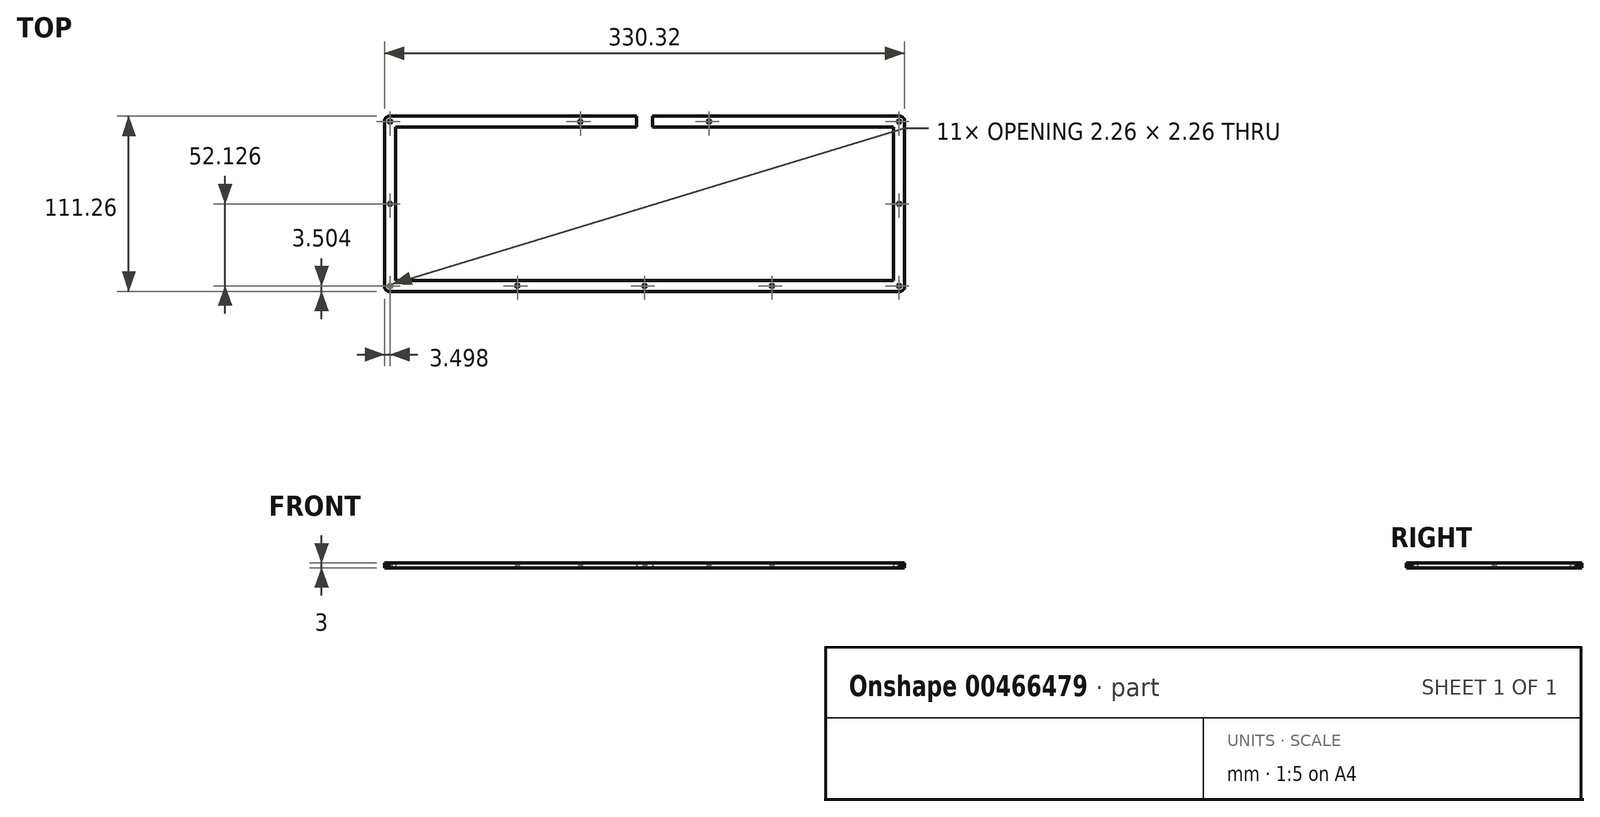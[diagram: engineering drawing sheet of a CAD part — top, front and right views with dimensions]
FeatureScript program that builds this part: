
annotation { "Feature Type Name" : "Feature", "Feature Type Description" : "" }
export const myFeature = defineFeature(function(context is Context, id is Id, definition is map)
    precondition{}
    {
        {
            var Q0;
            Q0=qCreatedBy(makeId("Top.planeOp"),FACE);
            var sketch = newSketch(context, id + "F0", { "sketchPlane" : qUnion([Q0])});
            skLineSegment(sketch, "E0", {"start": v(-5, 55.63) * mm, "end": v(-5, 48.62) * mm});
            skLineSegment(sketch, "E1", {"start": v(-5, 48.62) * mm, "end": v(-158.16, 48.62) * mm});
            skLineSegment(sketch, "E2", {"start": v(-158.16, 48.62) * mm, "end": v(-158.16, -48.63) * mm});
            skLineSegment(sketch, "E3", {"start": v(-158.16, -48.63) * mm, "end": v(158.16, -48.63) * mm});
            skLineSegment(sketch, "E4", {"start": v(158.16, -48.63) * mm, "end": v(158.16, 48.62) * mm});
            skLineSegment(sketch, "E5", {"start": v(158.16, 48.62) * mm, "end": v(5, 48.62) * mm});
            skLineSegment(sketch, "E6", {"start": v(5, 48.62) * mm, "end": v(5, 55.62) * mm});
            skLineSegment(sketch, "E7", {"start": v(5, 55.62) * mm, "end": v(162.16, 55.62) * mm});
            skLineSegment(sketch, "E8", {"start": v(162.16, 55.62) * mm, "end": v(162.4, 55.62) * mm});
            skLineSegment(sketch, "E9", {"start": v(162.4, 55.62) * mm, "end": v(162.63, 55.59) * mm});
            skLineSegment(sketch, "E10", {"start": v(162.63, 55.59) * mm, "end": v(162.86, 55.54) * mm});
            skLineSegment(sketch, "E11", {"start": v(162.86, 55.54) * mm, "end": v(163.1, 55.48) * mm});
            skLineSegment(sketch, "E12", {"start": v(163.1, 55.48) * mm, "end": v(163.31, 55.4) * mm});
            skLineSegment(sketch, "E13", {"start": v(163.31, 55.4) * mm, "end": v(163.53, 55.3) * mm});
            skLineSegment(sketch, "E14", {"start": v(163.53, 55.3) * mm, "end": v(163.73, 55.18) * mm});
            skLineSegment(sketch, "E15", {"start": v(163.73, 55.18) * mm, "end": v(163.93, 55.05) * mm});
            skLineSegment(sketch, "E16", {"start": v(163.93, 55.05) * mm, "end": v(164.11, 54.9) * mm});
            skLineSegment(sketch, "E17", {"start": v(164.11, 54.9) * mm, "end": v(164.29, 54.75) * mm});
            skLineSegment(sketch, "E18", {"start": v(164.29, 54.75) * mm, "end": v(164.45, 54.57) * mm});
            skLineSegment(sketch, "E19", {"start": v(164.45, 54.57) * mm, "end": v(164.6, 54.39) * mm});
            skLineSegment(sketch, "E20", {"start": v(164.6, 54.39) * mm, "end": v(164.72, 54.2) * mm});
            skLineSegment(sketch, "E21", {"start": v(164.72, 54.2) * mm, "end": v(164.84, 53.99) * mm});
            skLineSegment(sketch, "E22", {"start": v(164.84, 53.99) * mm, "end": v(164.93, 53.77) * mm});
            skLineSegment(sketch, "E23", {"start": v(164.93, 53.77) * mm, "end": v(165.02, 53.55) * mm});
            skLineSegment(sketch, "E24", {"start": v(165.02, 53.55) * mm, "end": v(165.08, 53.33) * mm});
            skLineSegment(sketch, "E25", {"start": v(165.08, 53.33) * mm, "end": v(165.13, 53.1) * mm});
            skLineSegment(sketch, "E26", {"start": v(165.13, 53.1) * mm, "end": v(165.15, 52.86) * mm});
            skLineSegment(sketch, "E27", {"start": v(165.15, 52.86) * mm, "end": v(165.16, 52.62) * mm});
            skLineSegment(sketch, "E28", {"start": v(165.16, 52.62) * mm, "end": v(165.16, -52.63) * mm});
            skLineSegment(sketch, "E29", {"start": v(165.16, -52.63) * mm, "end": v(165.15, -52.86) * mm});
            skLineSegment(sketch, "E30", {"start": v(165.15, -52.86) * mm, "end": v(165.13, -53.1) * mm});
            skLineSegment(sketch, "E31", {"start": v(165.13, -53.1) * mm, "end": v(165.08, -53.33) * mm});
            skLineSegment(sketch, "E32", {"start": v(165.08, -53.33) * mm, "end": v(165.02, -53.55) * mm});
            skLineSegment(sketch, "E33", {"start": v(165.02, -53.55) * mm, "end": v(164.93, -53.77) * mm});
            skLineSegment(sketch, "E34", {"start": v(164.93, -53.77) * mm, "end": v(164.84, -53.99) * mm});
            skLineSegment(sketch, "E35", {"start": v(164.84, -53.99) * mm, "end": v(164.72, -54.2) * mm});
            skLineSegment(sketch, "E36", {"start": v(164.72, -54.2) * mm, "end": v(164.6, -54.39) * mm});
            skLineSegment(sketch, "E37", {"start": v(164.6, -54.39) * mm, "end": v(164.45, -54.57) * mm});
            skLineSegment(sketch, "E38", {"start": v(164.45, -54.57) * mm, "end": v(164.29, -54.75) * mm});
            skLineSegment(sketch, "E39", {"start": v(164.29, -54.75) * mm, "end": v(164.11, -54.9) * mm});
            skLineSegment(sketch, "E40", {"start": v(164.11, -54.9) * mm, "end": v(163.93, -55.05) * mm});
            skLineSegment(sketch, "E41", {"start": v(163.93, -55.05) * mm, "end": v(163.73, -55.18) * mm});
            skLineSegment(sketch, "E42", {"start": v(163.73, -55.18) * mm, "end": v(163.53, -55.3) * mm});
            skLineSegment(sketch, "E43", {"start": v(163.53, -55.3) * mm, "end": v(163.31, -55.4) * mm});
            skLineSegment(sketch, "E44", {"start": v(163.31, -55.4) * mm, "end": v(163.1, -55.48) * mm});
            skLineSegment(sketch, "E45", {"start": v(163.1, -55.48) * mm, "end": v(162.86, -55.54) * mm});
            skLineSegment(sketch, "E46", {"start": v(162.86, -55.54) * mm, "end": v(162.63, -55.59) * mm});
            skLineSegment(sketch, "E47", {"start": v(162.63, -55.59) * mm, "end": v(162.4, -55.62) * mm});
            skLineSegment(sketch, "E48", {"start": v(162.4, -55.62) * mm, "end": v(162.16, -55.63) * mm});
            skLineSegment(sketch, "E49", {"start": v(162.16, -55.63) * mm, "end": v(-162.16, -55.63) * mm});
            skLineSegment(sketch, "E50", {"start": v(-162.16, -55.63) * mm, "end": v(-162.4, -55.62) * mm});
            skLineSegment(sketch, "E51", {"start": v(-162.4, -55.62) * mm, "end": v(-162.63, -55.59) * mm});
            skLineSegment(sketch, "E52", {"start": v(-162.63, -55.59) * mm, "end": v(-162.86, -55.54) * mm});
            skLineSegment(sketch, "E53", {"start": v(-162.86, -55.54) * mm, "end": v(-163.09, -55.48) * mm});
            skLineSegment(sketch, "E54", {"start": v(-163.09, -55.48) * mm, "end": v(-163.31, -55.4) * mm});
            skLineSegment(sketch, "E55", {"start": v(-163.31, -55.4) * mm, "end": v(-163.52, -55.3) * mm});
            skLineSegment(sketch, "E56", {"start": v(-163.52, -55.3) * mm, "end": v(-163.73, -55.18) * mm});
            skLineSegment(sketch, "E57", {"start": v(-163.73, -55.18) * mm, "end": v(-163.93, -55.05) * mm});
            skLineSegment(sketch, "E58", {"start": v(-163.93, -55.05) * mm, "end": v(-164.11, -54.9) * mm});
            skLineSegment(sketch, "E59", {"start": v(-164.11, -54.9) * mm, "end": v(-164.28, -54.75) * mm});
            skLineSegment(sketch, "E60", {"start": v(-164.28, -54.75) * mm, "end": v(-164.44, -54.57) * mm});
            skLineSegment(sketch, "E61", {"start": v(-164.44, -54.57) * mm, "end": v(-164.6, -54.39) * mm});
            skLineSegment(sketch, "E62", {"start": v(-164.6, -54.39) * mm, "end": v(-164.72, -54.2) * mm});
            skLineSegment(sketch, "E63", {"start": v(-164.72, -54.2) * mm, "end": v(-164.84, -53.99) * mm});
            skLineSegment(sketch, "E64", {"start": v(-164.84, -53.99) * mm, "end": v(-164.93, -53.77) * mm});
            skLineSegment(sketch, "E65", {"start": v(-164.93, -53.77) * mm, "end": v(-165.02, -53.55) * mm});
            skLineSegment(sketch, "E66", {"start": v(-165.02, -53.55) * mm, "end": v(-165.08, -53.33) * mm});
            skLineSegment(sketch, "E67", {"start": v(-165.08, -53.33) * mm, "end": v(-165.13, -53.1) * mm});
            skLineSegment(sketch, "E68", {"start": v(-165.13, -53.1) * mm, "end": v(-165.15, -52.86) * mm});
            skLineSegment(sketch, "E69", {"start": v(-165.15, -52.86) * mm, "end": v(-165.16, -52.63) * mm});
            skLineSegment(sketch, "E70", {"start": v(-165.16, -52.63) * mm, "end": v(-165.16, 52.62) * mm});
            skLineSegment(sketch, "E71", {"start": v(-165.16, 52.62) * mm, "end": v(-165.15, 52.86) * mm});
            skLineSegment(sketch, "E72", {"start": v(-165.15, 52.86) * mm, "end": v(-165.13, 53.1) * mm});
            skLineSegment(sketch, "E73", {"start": v(-165.13, 53.1) * mm, "end": v(-165.08, 53.33) * mm});
            skLineSegment(sketch, "E74", {"start": v(-165.08, 53.33) * mm, "end": v(-165.02, 53.55) * mm});
            skLineSegment(sketch, "E75", {"start": v(-165.02, 53.55) * mm, "end": v(-164.93, 53.77) * mm});
            skLineSegment(sketch, "E76", {"start": v(-164.93, 53.77) * mm, "end": v(-164.84, 53.99) * mm});
            skLineSegment(sketch, "E77", {"start": v(-164.84, 53.99) * mm, "end": v(-164.72, 54.2) * mm});
            skLineSegment(sketch, "E78", {"start": v(-164.72, 54.2) * mm, "end": v(-164.6, 54.39) * mm});
            skLineSegment(sketch, "E79", {"start": v(-164.6, 54.39) * mm, "end": v(-164.44, 54.57) * mm});
            skLineSegment(sketch, "E80", {"start": v(-164.44, 54.57) * mm, "end": v(-164.28, 54.75) * mm});
            skLineSegment(sketch, "E81", {"start": v(-164.28, 54.75) * mm, "end": v(-164.11, 54.9) * mm});
            skLineSegment(sketch, "E82", {"start": v(-164.11, 54.9) * mm, "end": v(-163.93, 55.05) * mm});
            skLineSegment(sketch, "E83", {"start": v(-163.93, 55.05) * mm, "end": v(-163.73, 55.18) * mm});
            skLineSegment(sketch, "E84", {"start": v(-163.73, 55.18) * mm, "end": v(-163.52, 55.3) * mm});
            skLineSegment(sketch, "E85", {"start": v(-163.52, 55.3) * mm, "end": v(-163.31, 55.4) * mm});
            skLineSegment(sketch, "E86", {"start": v(-163.31, 55.4) * mm, "end": v(-163.09, 55.48) * mm});
            skLineSegment(sketch, "E87", {"start": v(-163.09, 55.48) * mm, "end": v(-162.86, 55.54) * mm});
            skLineSegment(sketch, "E88", {"start": v(-162.86, 55.54) * mm, "end": v(-162.63, 55.59) * mm});
            skLineSegment(sketch, "E89", {"start": v(-162.63, 55.59) * mm, "end": v(-162.4, 55.62) * mm});
            skLineSegment(sketch, "E90", {"start": v(-162.4, 55.62) * mm, "end": v(-162.16, 55.63) * mm});
            skLineSegment(sketch, "E91", {"start": v(-162.16, 55.63) * mm, "end": v(-5, 55.63) * mm});
            skLineSegment(sketch, "E92", {"start": v(161.31, -51.05) * mm, "end": v(161, -51.21) * mm});
            skLineSegment(sketch, "E93", {"start": v(161, -51.21) * mm, "end": v(160.75, -51.46) * mm});
            skLineSegment(sketch, "E94", {"start": v(160.75, -51.46) * mm, "end": v(160.59, -51.78) * mm});
            skLineSegment(sketch, "E95", {"start": v(160.59, -51.78) * mm, "end": v(160.53, -52.13) * mm});
            skLineSegment(sketch, "E96", {"start": v(160.53, -52.13) * mm, "end": v(160.59, -52.48) * mm});
            skLineSegment(sketch, "E97", {"start": v(160.59, -52.48) * mm, "end": v(160.75, -52.79) * mm});
            skLineSegment(sketch, "E98", {"start": v(160.75, -52.79) * mm, "end": v(161, -53.04) * mm});
            skLineSegment(sketch, "E99", {"start": v(161, -53.04) * mm, "end": v(161.31, -53.2) * mm});
            skLineSegment(sketch, "E100", {"start": v(161.31, -53.2) * mm, "end": v(161.66, -53.26) * mm});
            skLineSegment(sketch, "E101", {"start": v(161.66, -53.26) * mm, "end": v(162.01, -53.2) * mm});
            skLineSegment(sketch, "E102", {"start": v(162.01, -53.2) * mm, "end": v(162.33, -53.04) * mm});
            skLineSegment(sketch, "E103", {"start": v(162.33, -53.04) * mm, "end": v(162.58, -52.79) * mm});
            skLineSegment(sketch, "E104", {"start": v(162.58, -52.79) * mm, "end": v(162.74, -52.48) * mm});
            skLineSegment(sketch, "E105", {"start": v(162.74, -52.48) * mm, "end": v(162.8, -52.13) * mm});
            skLineSegment(sketch, "E106", {"start": v(162.8, -52.13) * mm, "end": v(162.74, -51.78) * mm});
            skLineSegment(sketch, "E107", {"start": v(162.74, -51.78) * mm, "end": v(162.58, -51.46) * mm});
            skLineSegment(sketch, "E108", {"start": v(162.58, -51.46) * mm, "end": v(162.33, -51.21) * mm});
            skLineSegment(sketch, "E109", {"start": v(162.33, -51.21) * mm, "end": v(162.01, -51.05) * mm});
            skLineSegment(sketch, "E110", {"start": v(162.01, -51.05) * mm, "end": v(161.66, -51) * mm});
            skLineSegment(sketch, "E111", {"start": v(161.66, -51) * mm, "end": v(161.31, -51.05) * mm});
            skLineSegment(sketch, "E112", {"start": v(80.48, -51.05) * mm, "end": v(80.17, -51.21) * mm});
            skLineSegment(sketch, "E113", {"start": v(80.17, -51.21) * mm, "end": v(79.92, -51.46) * mm});
            skLineSegment(sketch, "E114", {"start": v(79.92, -51.46) * mm, "end": v(79.76, -51.78) * mm});
            skLineSegment(sketch, "E115", {"start": v(79.76, -51.78) * mm, "end": v(79.7, -52.13) * mm});
            skLineSegment(sketch, "E116", {"start": v(79.7, -52.13) * mm, "end": v(79.76, -52.48) * mm});
            skLineSegment(sketch, "E117", {"start": v(79.76, -52.48) * mm, "end": v(79.92, -52.79) * mm});
            skLineSegment(sketch, "E118", {"start": v(79.92, -52.79) * mm, "end": v(80.17, -53.04) * mm});
            skLineSegment(sketch, "E119", {"start": v(80.17, -53.04) * mm, "end": v(80.48, -53.2) * mm});
            skLineSegment(sketch, "E120", {"start": v(80.48, -53.2) * mm, "end": v(80.83, -53.26) * mm});
            skLineSegment(sketch, "E121", {"start": v(80.83, -53.26) * mm, "end": v(81.18, -53.2) * mm});
            skLineSegment(sketch, "E122", {"start": v(81.18, -53.2) * mm, "end": v(81.5, -53.04) * mm});
            skLineSegment(sketch, "E123", {"start": v(81.5, -53.04) * mm, "end": v(81.75, -52.79) * mm});
            skLineSegment(sketch, "E124", {"start": v(81.75, -52.79) * mm, "end": v(81.9, -52.48) * mm});
            skLineSegment(sketch, "E125", {"start": v(81.9, -52.48) * mm, "end": v(81.96, -52.13) * mm});
            skLineSegment(sketch, "E126", {"start": v(81.96, -52.13) * mm, "end": v(81.9, -51.78) * mm});
            skLineSegment(sketch, "E127", {"start": v(81.9, -51.78) * mm, "end": v(81.75, -51.46) * mm});
            skLineSegment(sketch, "E128", {"start": v(81.75, -51.46) * mm, "end": v(81.5, -51.21) * mm});
            skLineSegment(sketch, "E129", {"start": v(81.5, -51.21) * mm, "end": v(81.18, -51.05) * mm});
            skLineSegment(sketch, "E130", {"start": v(81.18, -51.05) * mm, "end": v(80.83, -51) * mm});
            skLineSegment(sketch, "E131", {"start": v(80.83, -51) * mm, "end": v(80.48, -51.05) * mm});
            skLineSegment(sketch, "E132", {"start": v(-0.35, -51.05) * mm, "end": v(-0.66, -51.21) * mm});
            skLineSegment(sketch, "E133", {"start": v(-0.66, -51.21) * mm, "end": v(-0.91, -51.46) * mm});
            skLineSegment(sketch, "E134", {"start": v(-0.91, -51.46) * mm, "end": v(-1.07, -51.78) * mm});
            skLineSegment(sketch, "E135", {"start": v(-1.07, -51.78) * mm, "end": v(-1.13, -52.13) * mm});
            skLineSegment(sketch, "E136", {"start": v(-1.13, -52.13) * mm, "end": v(-1.07, -52.48) * mm});
            skLineSegment(sketch, "E137", {"start": v(-1.07, -52.48) * mm, "end": v(-0.91, -52.79) * mm});
            skLineSegment(sketch, "E138", {"start": v(-0.91, -52.79) * mm, "end": v(-0.66, -53.04) * mm});
            skLineSegment(sketch, "E139", {"start": v(-0.66, -53.04) * mm, "end": v(-0.35, -53.2) * mm});
            skLineSegment(sketch, "E140", {"start": v(-0.35, -53.2) * mm, "end": v(0, -53.26) * mm});
            skLineSegment(sketch, "E141", {"start": v(0, -53.26) * mm, "end": v(0.35, -53.2) * mm});
            skLineSegment(sketch, "E142", {"start": v(0.35, -53.2) * mm, "end": v(0.67, -53.04) * mm});
            skLineSegment(sketch, "E143", {"start": v(0.67, -53.04) * mm, "end": v(0.92, -52.79) * mm});
            skLineSegment(sketch, "E144", {"start": v(0.92, -52.79) * mm, "end": v(1.07, -52.48) * mm});
            skLineSegment(sketch, "E145", {"start": v(1.07, -52.48) * mm, "end": v(1.13, -52.13) * mm});
            skLineSegment(sketch, "E146", {"start": v(1.13, -52.13) * mm, "end": v(1.07, -51.78) * mm});
            skLineSegment(sketch, "E147", {"start": v(1.07, -51.78) * mm, "end": v(0.92, -51.46) * mm});
            skLineSegment(sketch, "E148", {"start": v(0.92, -51.46) * mm, "end": v(0.67, -51.21) * mm});
            skLineSegment(sketch, "E149", {"start": v(0.67, -51.21) * mm, "end": v(0.35, -51.05) * mm});
            skLineSegment(sketch, "E150", {"start": v(0.35, -51.05) * mm, "end": v(0, -51) * mm});
            skLineSegment(sketch, "E151", {"start": v(0, -51) * mm, "end": v(-0.35, -51.05) * mm});
            skLineSegment(sketch, "E152", {"start": v(-81.18, -51.05) * mm, "end": v(-81.5, -51.21) * mm});
            skLineSegment(sketch, "E153", {"start": v(-81.5, -51.21) * mm, "end": v(-81.75, -51.46) * mm});
            skLineSegment(sketch, "E154", {"start": v(-81.75, -51.46) * mm, "end": v(-81.9, -51.78) * mm});
            skLineSegment(sketch, "E155", {"start": v(-81.9, -51.78) * mm, "end": v(-81.96, -52.13) * mm});
            skLineSegment(sketch, "E156", {"start": v(-81.96, -52.13) * mm, "end": v(-81.9, -52.48) * mm});
            skLineSegment(sketch, "E157", {"start": v(-81.9, -52.48) * mm, "end": v(-81.75, -52.79) * mm});
            skLineSegment(sketch, "E158", {"start": v(-81.75, -52.79) * mm, "end": v(-81.5, -53.04) * mm});
            skLineSegment(sketch, "E159", {"start": v(-81.5, -53.04) * mm, "end": v(-81.18, -53.2) * mm});
            skLineSegment(sketch, "E160", {"start": v(-81.18, -53.2) * mm, "end": v(-80.83, -53.26) * mm});
            skLineSegment(sketch, "E161", {"start": v(-80.83, -53.26) * mm, "end": v(-80.48, -53.2) * mm});
            skLineSegment(sketch, "E162", {"start": v(-80.48, -53.2) * mm, "end": v(-80.17, -53.04) * mm});
            skLineSegment(sketch, "E163", {"start": v(-80.17, -53.04) * mm, "end": v(-79.92, -52.79) * mm});
            skLineSegment(sketch, "E164", {"start": v(-79.92, -52.79) * mm, "end": v(-79.76, -52.48) * mm});
            skLineSegment(sketch, "E165", {"start": v(-79.76, -52.48) * mm, "end": v(-79.7, -52.13) * mm});
            skLineSegment(sketch, "E166", {"start": v(-79.7, -52.13) * mm, "end": v(-79.76, -51.78) * mm});
            skLineSegment(sketch, "E167", {"start": v(-79.76, -51.78) * mm, "end": v(-79.92, -51.46) * mm});
            skLineSegment(sketch, "E168", {"start": v(-79.92, -51.46) * mm, "end": v(-80.17, -51.21) * mm});
            skLineSegment(sketch, "E169", {"start": v(-80.17, -51.21) * mm, "end": v(-80.48, -51.05) * mm});
            skLineSegment(sketch, "E170", {"start": v(-80.48, -51.05) * mm, "end": v(-80.83, -51) * mm});
            skLineSegment(sketch, "E171", {"start": v(-80.83, -51) * mm, "end": v(-81.18, -51.05) * mm});
            skLineSegment(sketch, "E172", {"start": v(-162.01, -51.05) * mm, "end": v(-162.33, -51.21) * mm});
            skLineSegment(sketch, "E173", {"start": v(-162.33, -51.21) * mm, "end": v(-162.58, -51.46) * mm});
            skLineSegment(sketch, "E174", {"start": v(-162.58, -51.46) * mm, "end": v(-162.74, -51.78) * mm});
            skLineSegment(sketch, "E175", {"start": v(-162.74, -51.78) * mm, "end": v(-162.8, -52.13) * mm});
            skLineSegment(sketch, "E176", {"start": v(-162.8, -52.13) * mm, "end": v(-162.74, -52.48) * mm});
            skLineSegment(sketch, "E177", {"start": v(-162.74, -52.48) * mm, "end": v(-162.58, -52.79) * mm});
            skLineSegment(sketch, "E178", {"start": v(-162.58, -52.79) * mm, "end": v(-162.33, -53.04) * mm});
            skLineSegment(sketch, "E179", {"start": v(-162.33, -53.04) * mm, "end": v(-162.01, -53.2) * mm});
            skLineSegment(sketch, "E180", {"start": v(-162.01, -53.2) * mm, "end": v(-161.66, -53.26) * mm});
            skLineSegment(sketch, "E181", {"start": v(-161.66, -53.26) * mm, "end": v(-161.31, -53.2) * mm});
            skLineSegment(sketch, "E182", {"start": v(-161.31, -53.2) * mm, "end": v(-161, -53.04) * mm});
            skLineSegment(sketch, "E183", {"start": v(-161, -53.04) * mm, "end": v(-160.75, -52.79) * mm});
            skLineSegment(sketch, "E184", {"start": v(-160.75, -52.79) * mm, "end": v(-160.59, -52.48) * mm});
            skLineSegment(sketch, "E185", {"start": v(-160.59, -52.48) * mm, "end": v(-160.53, -52.13) * mm});
            skLineSegment(sketch, "E186", {"start": v(-160.53, -52.13) * mm, "end": v(-160.59, -51.78) * mm});
            skLineSegment(sketch, "E187", {"start": v(-160.59, -51.78) * mm, "end": v(-160.75, -51.46) * mm});
            skLineSegment(sketch, "E188", {"start": v(-160.75, -51.46) * mm, "end": v(-161, -51.21) * mm});
            skLineSegment(sketch, "E189", {"start": v(-161, -51.21) * mm, "end": v(-161.31, -51.05) * mm});
            skLineSegment(sketch, "E190", {"start": v(-161.31, -51.05) * mm, "end": v(-161.66, -51) * mm});
            skLineSegment(sketch, "E191", {"start": v(-161.66, -51) * mm, "end": v(-162.01, -51.05) * mm});
            skLineSegment(sketch, "E192", {"start": v(161.31, 1.08) * mm, "end": v(161, 0.91) * mm});
            skLineSegment(sketch, "E193", {"start": v(161, 0.91) * mm, "end": v(160.75, 0.66) * mm});
            skLineSegment(sketch, "E194", {"start": v(160.75, 0.66) * mm, "end": v(160.59, 0.35) * mm});
            skLineSegment(sketch, "E195", {"start": v(160.59, 0.35) * mm, "end": v(160.53, 0) * mm});
            skLineSegment(sketch, "E196", {"start": v(160.53, 0) * mm, "end": v(160.59, -0.35) * mm});
            skLineSegment(sketch, "E197", {"start": v(160.59, -0.35) * mm, "end": v(160.75, -0.66) * mm});
            skLineSegment(sketch, "E198", {"start": v(160.75, -0.66) * mm, "end": v(161, -0.91) * mm});
            skLineSegment(sketch, "E199", {"start": v(161, -0.91) * mm, "end": v(161.31, -1.07) * mm});
            skLineSegment(sketch, "E200", {"start": v(161.31, -1.07) * mm, "end": v(161.66, -1.13) * mm});
            skLineSegment(sketch, "E201", {"start": v(161.66, -1.13) * mm, "end": v(162.01, -1.07) * mm});
            skLineSegment(sketch, "E202", {"start": v(162.01, -1.07) * mm, "end": v(162.33, -0.91) * mm});
            skLineSegment(sketch, "E203", {"start": v(162.33, -0.91) * mm, "end": v(162.58, -0.66) * mm});
            skLineSegment(sketch, "E204", {"start": v(162.58, -0.66) * mm, "end": v(162.74, -0.35) * mm});
            skLineSegment(sketch, "E205", {"start": v(162.74, -0.35) * mm, "end": v(162.8, 0) * mm});
            skLineSegment(sketch, "E206", {"start": v(162.8, 0) * mm, "end": v(162.74, 0.35) * mm});
            skLineSegment(sketch, "E207", {"start": v(162.74, 0.35) * mm, "end": v(162.58, 0.66) * mm});
            skLineSegment(sketch, "E208", {"start": v(162.58, 0.66) * mm, "end": v(162.33, 0.91) * mm});
            skLineSegment(sketch, "E209", {"start": v(162.33, 0.91) * mm, "end": v(162.01, 1.08) * mm});
            skLineSegment(sketch, "E210", {"start": v(162.01, 1.08) * mm, "end": v(161.66, 1.13) * mm});
            skLineSegment(sketch, "E211", {"start": v(161.66, 1.13) * mm, "end": v(161.31, 1.08) * mm});
            skLineSegment(sketch, "E212", {"start": v(-162.01, 1.08) * mm, "end": v(-162.33, 0.91) * mm});
            skLineSegment(sketch, "E213", {"start": v(-162.33, 0.91) * mm, "end": v(-162.58, 0.66) * mm});
            skLineSegment(sketch, "E214", {"start": v(-162.58, 0.66) * mm, "end": v(-162.74, 0.35) * mm});
            skLineSegment(sketch, "E215", {"start": v(-162.74, 0.35) * mm, "end": v(-162.8, 0) * mm});
            skLineSegment(sketch, "E216", {"start": v(-162.8, 0) * mm, "end": v(-162.74, -0.35) * mm});
            skLineSegment(sketch, "E217", {"start": v(-162.74, -0.35) * mm, "end": v(-162.58, -0.66) * mm});
            skLineSegment(sketch, "E218", {"start": v(-162.58, -0.66) * mm, "end": v(-162.33, -0.91) * mm});
            skLineSegment(sketch, "E219", {"start": v(-162.33, -0.91) * mm, "end": v(-162.01, -1.07) * mm});
            skLineSegment(sketch, "E220", {"start": v(-162.01, -1.07) * mm, "end": v(-161.66, -1.13) * mm});
            skLineSegment(sketch, "E221", {"start": v(-161.66, -1.13) * mm, "end": v(-161.31, -1.07) * mm});
            skLineSegment(sketch, "E222", {"start": v(-161.31, -1.07) * mm, "end": v(-161, -0.91) * mm});
            skLineSegment(sketch, "E223", {"start": v(-161, -0.91) * mm, "end": v(-160.75, -0.66) * mm});
            skLineSegment(sketch, "E224", {"start": v(-160.75, -0.66) * mm, "end": v(-160.59, -0.35) * mm});
            skLineSegment(sketch, "E225", {"start": v(-160.59, -0.35) * mm, "end": v(-160.53, 0) * mm});
            skLineSegment(sketch, "E226", {"start": v(-160.53, 0) * mm, "end": v(-160.59, 0.35) * mm});
            skLineSegment(sketch, "E227", {"start": v(-160.59, 0.35) * mm, "end": v(-160.75, 0.66) * mm});
            skLineSegment(sketch, "E228", {"start": v(-160.75, 0.66) * mm, "end": v(-161, 0.91) * mm});
            skLineSegment(sketch, "E229", {"start": v(-161, 0.91) * mm, "end": v(-161.31, 1.08) * mm});
            skLineSegment(sketch, "E230", {"start": v(-161.31, 1.08) * mm, "end": v(-161.66, 1.13) * mm});
            skLineSegment(sketch, "E231", {"start": v(-161.66, 1.13) * mm, "end": v(-162.01, 1.08) * mm});
            skLineSegment(sketch, "E232", {"start": v(-41.18, 53.2) * mm, "end": v(-41.5, 53.04) * mm});
            skLineSegment(sketch, "E233", {"start": v(-41.5, 53.04) * mm, "end": v(-41.75, 52.8) * mm});
            skLineSegment(sketch, "E234", {"start": v(-41.75, 52.8) * mm, "end": v(-41.9, 52.47) * mm});
            skLineSegment(sketch, "E235", {"start": v(-41.9, 52.47) * mm, "end": v(-41.96, 52.12) * mm});
            skLineSegment(sketch, "E236", {"start": v(-41.96, 52.12) * mm, "end": v(-41.9, 51.78) * mm});
            skLineSegment(sketch, "E237", {"start": v(-41.9, 51.78) * mm, "end": v(-41.75, 51.46) * mm});
            skLineSegment(sketch, "E238", {"start": v(-41.75, 51.46) * mm, "end": v(-41.5, 51.21) * mm});
            skLineSegment(sketch, "E239", {"start": v(-41.5, 51.21) * mm, "end": v(-41.18, 51.05) * mm});
            skLineSegment(sketch, "E240", {"start": v(-41.18, 51.05) * mm, "end": v(-40.83, 51) * mm});
            skLineSegment(sketch, "E241", {"start": v(-40.83, 51) * mm, "end": v(-40.48, 51.05) * mm});
            skLineSegment(sketch, "E242", {"start": v(-40.48, 51.05) * mm, "end": v(-40.17, 51.21) * mm});
            skLineSegment(sketch, "E243", {"start": v(-40.17, 51.21) * mm, "end": v(-39.92, 51.46) * mm});
            skLineSegment(sketch, "E244", {"start": v(-39.92, 51.46) * mm, "end": v(-39.76, 51.78) * mm});
            skLineSegment(sketch, "E245", {"start": v(-39.76, 51.78) * mm, "end": v(-39.7, 52.12) * mm});
            skLineSegment(sketch, "E246", {"start": v(-39.7, 52.12) * mm, "end": v(-39.76, 52.47) * mm});
            skLineSegment(sketch, "E247", {"start": v(-39.76, 52.47) * mm, "end": v(-39.92, 52.8) * mm});
            skLineSegment(sketch, "E248", {"start": v(-39.92, 52.8) * mm, "end": v(-40.17, 53.04) * mm});
            skLineSegment(sketch, "E249", {"start": v(-40.17, 53.04) * mm, "end": v(-40.48, 53.2) * mm});
            skLineSegment(sketch, "E250", {"start": v(-40.48, 53.2) * mm, "end": v(-40.83, 53.26) * mm});
            skLineSegment(sketch, "E251", {"start": v(-40.83, 53.26) * mm, "end": v(-41.18, 53.2) * mm});
            skLineSegment(sketch, "E252", {"start": v(40.48, 53.2) * mm, "end": v(40.17, 53.04) * mm});
            skLineSegment(sketch, "E253", {"start": v(40.17, 53.04) * mm, "end": v(39.92, 52.8) * mm});
            skLineSegment(sketch, "E254", {"start": v(39.92, 52.8) * mm, "end": v(39.76, 52.47) * mm});
            skLineSegment(sketch, "E255", {"start": v(39.76, 52.47) * mm, "end": v(39.7, 52.12) * mm});
            skLineSegment(sketch, "E256", {"start": v(39.7, 52.12) * mm, "end": v(39.76, 51.78) * mm});
            skLineSegment(sketch, "E257", {"start": v(39.76, 51.78) * mm, "end": v(39.92, 51.46) * mm});
            skLineSegment(sketch, "E258", {"start": v(39.92, 51.46) * mm, "end": v(40.17, 51.21) * mm});
            skLineSegment(sketch, "E259", {"start": v(40.17, 51.21) * mm, "end": v(40.48, 51.05) * mm});
            skLineSegment(sketch, "E260", {"start": v(40.48, 51.05) * mm, "end": v(40.83, 51) * mm});
            skLineSegment(sketch, "E261", {"start": v(40.83, 51) * mm, "end": v(41.18, 51.05) * mm});
            skLineSegment(sketch, "E262", {"start": v(41.18, 51.05) * mm, "end": v(41.5, 51.21) * mm});
            skLineSegment(sketch, "E263", {"start": v(41.5, 51.21) * mm, "end": v(41.75, 51.46) * mm});
            skLineSegment(sketch, "E264", {"start": v(41.75, 51.46) * mm, "end": v(41.9, 51.78) * mm});
            skLineSegment(sketch, "E265", {"start": v(41.9, 51.78) * mm, "end": v(41.96, 52.12) * mm});
            skLineSegment(sketch, "E266", {"start": v(41.96, 52.12) * mm, "end": v(41.9, 52.47) * mm});
            skLineSegment(sketch, "E267", {"start": v(41.9, 52.47) * mm, "end": v(41.75, 52.8) * mm});
            skLineSegment(sketch, "E268", {"start": v(41.75, 52.8) * mm, "end": v(41.5, 53.04) * mm});
            skLineSegment(sketch, "E269", {"start": v(41.5, 53.04) * mm, "end": v(41.18, 53.2) * mm});
            skLineSegment(sketch, "E270", {"start": v(41.18, 53.2) * mm, "end": v(40.83, 53.26) * mm});
            skLineSegment(sketch, "E271", {"start": v(40.83, 53.26) * mm, "end": v(40.48, 53.2) * mm});
            skLineSegment(sketch, "E272", {"start": v(161.31, 53.2) * mm, "end": v(161, 53.04) * mm});
            skLineSegment(sketch, "E273", {"start": v(161, 53.04) * mm, "end": v(160.75, 52.8) * mm});
            skLineSegment(sketch, "E274", {"start": v(160.75, 52.8) * mm, "end": v(160.59, 52.47) * mm});
            skLineSegment(sketch, "E275", {"start": v(160.59, 52.47) * mm, "end": v(160.53, 52.12) * mm});
            skLineSegment(sketch, "E276", {"start": v(160.53, 52.12) * mm, "end": v(160.59, 51.78) * mm});
            skLineSegment(sketch, "E277", {"start": v(160.59, 51.78) * mm, "end": v(160.75, 51.46) * mm});
            skLineSegment(sketch, "E278", {"start": v(160.75, 51.46) * mm, "end": v(161, 51.21) * mm});
            skLineSegment(sketch, "E279", {"start": v(161, 51.21) * mm, "end": v(161.31, 51.05) * mm});
            skLineSegment(sketch, "E280", {"start": v(161.31, 51.05) * mm, "end": v(161.66, 51) * mm});
            skLineSegment(sketch, "E281", {"start": v(161.66, 51) * mm, "end": v(162.01, 51.05) * mm});
            skLineSegment(sketch, "E282", {"start": v(162.01, 51.05) * mm, "end": v(162.33, 51.21) * mm});
            skLineSegment(sketch, "E283", {"start": v(162.33, 51.21) * mm, "end": v(162.58, 51.46) * mm});
            skLineSegment(sketch, "E284", {"start": v(162.58, 51.46) * mm, "end": v(162.74, 51.78) * mm});
            skLineSegment(sketch, "E285", {"start": v(162.74, 51.78) * mm, "end": v(162.8, 52.12) * mm});
            skLineSegment(sketch, "E286", {"start": v(162.8, 52.12) * mm, "end": v(162.74, 52.47) * mm});
            skLineSegment(sketch, "E287", {"start": v(162.74, 52.47) * mm, "end": v(162.58, 52.8) * mm});
            skLineSegment(sketch, "E288", {"start": v(162.58, 52.8) * mm, "end": v(162.33, 53.04) * mm});
            skLineSegment(sketch, "E289", {"start": v(162.33, 53.04) * mm, "end": v(162.01, 53.2) * mm});
            skLineSegment(sketch, "E290", {"start": v(162.01, 53.2) * mm, "end": v(161.66, 53.26) * mm});
            skLineSegment(sketch, "E291", {"start": v(161.66, 53.26) * mm, "end": v(161.31, 53.2) * mm});
            skLineSegment(sketch, "E292", {"start": v(-162.01, 53.2) * mm, "end": v(-162.33, 53.04) * mm});
            skLineSegment(sketch, "E293", {"start": v(-162.33, 53.04) * mm, "end": v(-162.58, 52.8) * mm});
            skLineSegment(sketch, "E294", {"start": v(-162.58, 52.8) * mm, "end": v(-162.74, 52.47) * mm});
            skLineSegment(sketch, "E295", {"start": v(-162.74, 52.47) * mm, "end": v(-162.8, 52.12) * mm});
            skLineSegment(sketch, "E296", {"start": v(-162.8, 52.12) * mm, "end": v(-162.74, 51.78) * mm});
            skLineSegment(sketch, "E297", {"start": v(-162.74, 51.78) * mm, "end": v(-162.58, 51.46) * mm});
            skLineSegment(sketch, "E298", {"start": v(-162.58, 51.46) * mm, "end": v(-162.33, 51.21) * mm});
            skLineSegment(sketch, "E299", {"start": v(-162.33, 51.21) * mm, "end": v(-162.01, 51.05) * mm});
            skLineSegment(sketch, "E300", {"start": v(-162.01, 51.05) * mm, "end": v(-161.66, 51) * mm});
            skLineSegment(sketch, "E301", {"start": v(-161.66, 51) * mm, "end": v(-161.31, 51.05) * mm});
            skLineSegment(sketch, "E302", {"start": v(-161.31, 51.05) * mm, "end": v(-161, 51.21) * mm});
            skLineSegment(sketch, "E303", {"start": v(-161, 51.21) * mm, "end": v(-160.75, 51.46) * mm});
            skLineSegment(sketch, "E304", {"start": v(-160.75, 51.46) * mm, "end": v(-160.59, 51.78) * mm});
            skLineSegment(sketch, "E305", {"start": v(-160.59, 51.78) * mm, "end": v(-160.53, 52.12) * mm});
            skLineSegment(sketch, "E306", {"start": v(-160.53, 52.12) * mm, "end": v(-160.59, 52.47) * mm});
            skLineSegment(sketch, "E307", {"start": v(-160.59, 52.47) * mm, "end": v(-160.75, 52.8) * mm});
            skLineSegment(sketch, "E308", {"start": v(-160.75, 52.8) * mm, "end": v(-161, 53.04) * mm});
            skLineSegment(sketch, "E309", {"start": v(-161, 53.04) * mm, "end": v(-161.31, 53.2) * mm});
            skLineSegment(sketch, "E310", {"start": v(-161.31, 53.2) * mm, "end": v(-161.66, 53.26) * mm});
            skLineSegment(sketch, "E311", {"start": v(-161.66, 53.26) * mm, "end": v(-162.01, 53.2) * mm});
            skSolve(sketch);
        }
        {
            var Q0;
            Q0=qSketchRegion(id+"F0",true);
            extrude(context, id + "F1", {"entities" : qUnion([Q0]), "depth" : 3 * mm});
        }
    });
